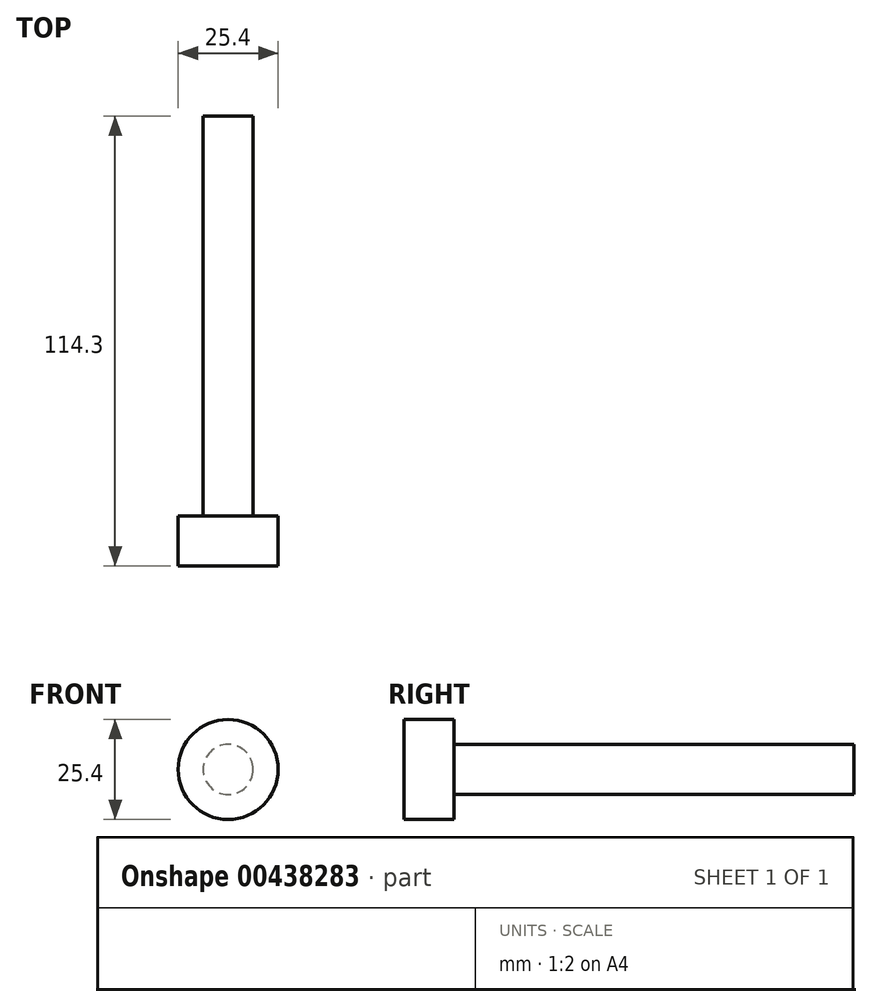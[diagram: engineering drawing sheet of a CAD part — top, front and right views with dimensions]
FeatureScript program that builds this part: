
annotation { "Feature Type Name" : "Feature", "Feature Type Description" : "" }
export const myFeature = defineFeature(function(context is Context, id is Id, definition is map)
    precondition{}
    {
        {
            var Q0;
            Q0=qCreatedBy(makeId("Front.planeOp"),FACE);
            var sketch = newSketch(context, id + "F0", { "sketchPlane" : qUnion([Q0])});
            skCircle(sketch, "E0", {"center": v(0, 6.35) * mm, "radius": 6.35 * mm});
            skSolve(sketch);
        }
        {
            var Q0;
            Q0=makeQuery(id+"F0.imprint","IMPRINT",FACE,{"disambiguationData":[TD([[makeQuery(id+"F0.imprint","IMPRINT",EDGE,{"derivedFrom":sQuery(id+"F0.wireOp",EDGE,"E0")}),1.0]])]});
            extrude(context, id + "F1", {"entities" : qUnion([Q0]), "depth" : 101.6 * mm});
        }
        {
            var Q0;
            Q0=makeQuery(id+"F1.opExtrude","CAP_FACE",FACE,{"disambiguationData":[OSD([sQuery(id+"F0.wireOp",EDGE,"E0")])],"isStart":false});
            var sketch = newSketch(context, id + "F2", { "sketchPlane" : qUnion([Q0])});
            skCircle(sketch, "E1", {"center": v(0, 6.35) * mm, "radius": 12.7 * mm});
            skSolve(sketch);
        }
        {
            var Q0;
            Q0=makeQuery(id+"F1.opExtrude","CAP_FACE",FACE,{"disambiguationData":[OSD([sQuery(id+"F0.wireOp",EDGE,"E0")])],"isStart":true});
            var Q1;
            Q1=makeQuery(id+"F2.imprint","IMPRINT",FACE,{"disambiguationData":[TD([[makeQuery(id+"F2.imprint","IMPRINT",EDGE,{"derivedFrom":sQuery(id+"F2.wireOp",EDGE,"E1")}),1.0]])]});
            var Q2;
            Q2=makeQuery(id+"F2.imprint","IMPRINT",FACE,{"disambiguationData":[TD([[makeQuery(id+"F2.imprint","IMPRINT",EDGE,{"derivedFrom":makeQuery(id+"F1.opExtrude","CAP_EDGE",EDGE,{"disambiguationData":[OSD([sQuery(id+"F0.wireOp",EDGE,"E0")])],"isStart":false})}),1.0]])]});
            var Q3;
            Q3=makeQuery(id+"F1.opExtrude","CAP_FACE",FACE,{"disambiguationData":[OSD([sQuery(id+"F0.wireOp",EDGE,"E0")])],"isStart":false});
            extrude(context, id + "F3", {"entities" : qUnion([Q0, Q1, Q2, Q3]), "operationType" : NewBodyOperationType.ADD, "endBound" : BoundingType.SYMMETRIC, "oppositeDirection" : true, "depth" : 12.7 * mm});
        }
        {
            var Q0;
            Q0=makeQuery(id+"F1.opExtrude","SWEPT_BODY",BODY,{"disambiguationData":[OSD([sQuery(id+"F0.wireOp",EDGE,"E0")])]});
            transform(context, id + "F4", {"entities" : qUnion([Q0]), "transformType" : TransformType.TRANSLATION_3D, "dx" : 0 * mm, "dy" : 47.75 * mm, "dz" : 0 * mm, "makeCopy" : false});
        }
    });
